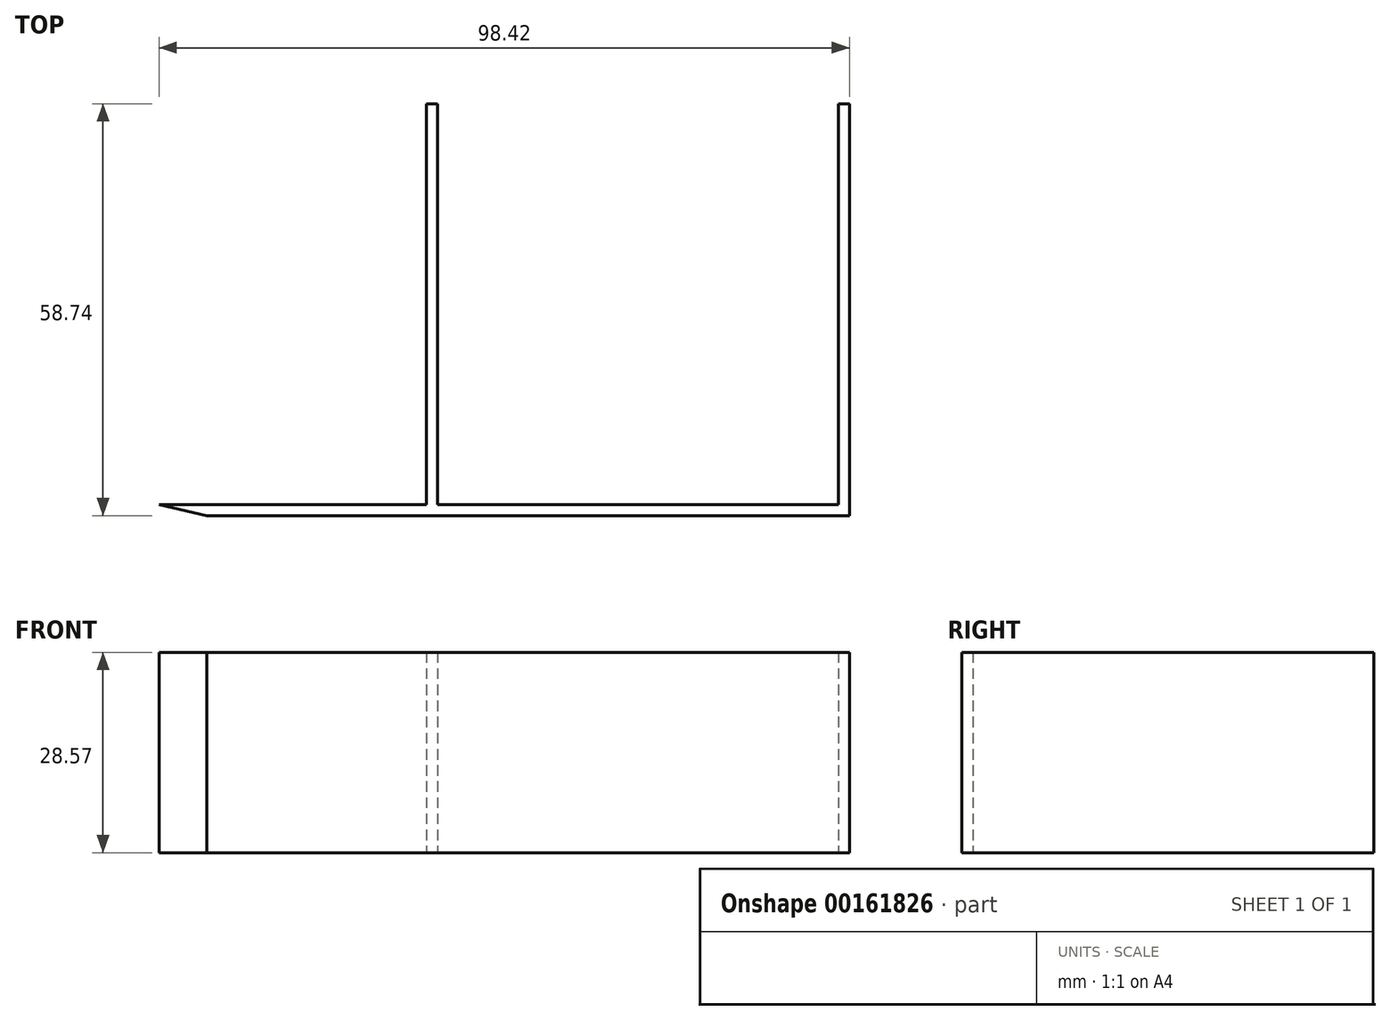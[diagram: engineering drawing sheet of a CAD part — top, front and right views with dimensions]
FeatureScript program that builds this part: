
annotation { "Feature Type Name" : "Feature", "Feature Type Description" : "" }
export const myFeature = defineFeature(function(context is Context, id is Id, definition is map)
    precondition{}
    {
        {
            var Q0;
            Q0=qCreatedBy(makeId("Top.planeOp"),FACE);
            var sketch = newSketch(context, id + "F0", { "sketchPlane" : qUnion([Q0])});
            skLineSegment(sketch, "E0", {"start": v(0, 0) * mm, "end": v(38.1, 0) * mm});
            skLineSegment(sketch, "E1", {"start": v(38.1, 0) * mm, "end": v(38.1, 57.15) * mm});
            skLineSegment(sketch, "E2", {"start": v(38.1, 57.15) * mm, "end": v(39.69, 57.15) * mm});
            skLineSegment(sketch, "E3", {"start": v(6.82, -1.59) * mm, "end": v(98.42, -1.59) * mm});
            skLineSegment(sketch, "E4", {"start": v(98.42, -1.59) * mm, "end": v(98.42, 57.15) * mm});
            skLineSegment(sketch, "E5", {"start": v(98.43, 57.15) * mm, "end": v(96.84, 57.15) * mm});
            skLineSegment(sketch, "E6", {"start": v(39.69, 57.15) * mm, "end": v(39.69, 0) * mm});
            skLineSegment(sketch, "E7", {"start": v(39.69, 0) * mm, "end": v(96.84, 0) * mm});
            skLineSegment(sketch, "E8", {"start": v(96.84, 0) * mm, "end": v(96.84, 57.15) * mm});
            skLineSegment(sketch, "E9", {"start": v(0, 0) * mm, "end": v(6.82, -1.59) * mm});
            skSolve(sketch);
        }
        {
            var Q0;
            Q0 = qSketchRegion(id + "F0", true);
            extrude(context, id + "F1", {"entities" : qUnion([Q0]), "depth" : 28.57 * mm});
        }
    });
